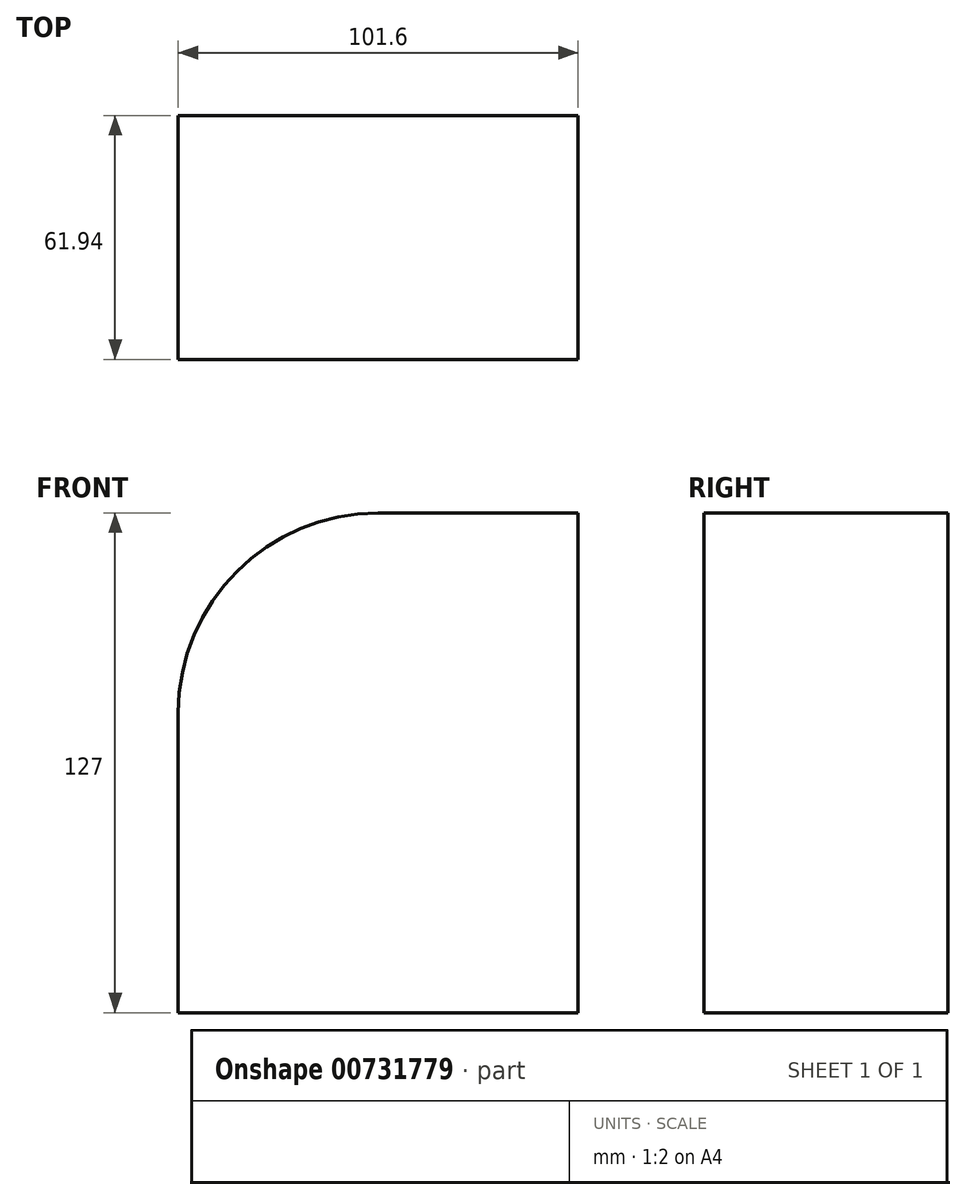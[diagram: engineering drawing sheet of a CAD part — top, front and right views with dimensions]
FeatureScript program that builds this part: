
annotation { "Feature Type Name" : "Feature", "Feature Type Description" : "" }
export const myFeature = defineFeature(function(context is Context, id is Id, definition is map)
    precondition{}
    {
        {
            var Q0;
            Q0=qCreatedBy(makeId("Front.planeOp"),FACE);
            var sketch = newSketch(context, id + "F0", { "sketchPlane" : qUnion([Q0])});
            skLineSegment(sketch, "E0.bottom", {"start": v(35.66, 104.35) * mm, "end": v(86.46, 104.35) * mm});
            skLineSegment(sketch, "E0.top", {"start": v(-15.14, -22.65) * mm, "end": v(86.46, -22.65) * mm});
            skLineSegment(sketch, "E0.left", {"start": v(-15.14, 53.55) * mm, "end": v(-15.14, -22.65) * mm});
            skLineSegment(sketch, "E0.right", {"start": v(86.46, 104.35) * mm, "end": v(86.46, -22.65) * mm});
            skPoint(sketch, "E1.visualSharp", {"position": v(-15.14, 104.35) * mm});
            skArc(sketch, "E1.filletArc", {"start": v(35.66, 104.35) * mm, "mid": v(-0.26, 89.47) * mm, "end": v(-15.14, 53.55) * mm});
            skSolve(sketch);
        }
        {
            var Q0;
            Q0=qSketchRegion(id+"F0",true);
            var Q1;
            Q1=qBodyType(qCreatedBy(id+"F0",EDGE),BodyType.WIRE);
            extrude(context, id + "F1", {"entities" : qUnion([Q0]), "surfaceEntities" : qUnion([Q1]), "depth" : 61.94 * mm, "offsetDistance" : 25.4 * mm});
        }
    });
